# Revit family: Framery One Compact
name_source: partatom
category: Furniture Systems
units: mm (PartAtom-declared; Revit-internal decimal feet)

## family parameters
Always vertical = Yes
Cut with Voids When Loaded = No
Part Type = Normal
Room Calculation Point = No
Round Connector Dimension = Use Diameter
Shared = No
Work Plane-Based = No

## types (2) — shared parameters
Assembly Code = 5111
Keynote = 8192
Manufacturer = Framery Oy
TD_Area_ = 1.03 m²
TD_BIM_content_publish_Revit_version_ = Revit 2021.1.9
TD_BIM_content_publish_date_ = 26.02.2024
TD_Collection_name_ = Framery One Compact
TD_Depth_ = 1000 mm  [stored 3.28084 ft]
TD_Height_ = 2255 mm  [stored 7.39829 ft]
TD_Product_category_ = Office pods
TD_Weight_ = 357.00 kg
TD_Width_ = 1030 mm  [stored 3.37927 ft]
zero-valued in all types: Default Elevation

## per-type parameters (varying)
| type | Framery_Height_adjustable_seat_ | Framery_Highpower_USB_C_ | Framery_LAN_ | Model | TD_Additional_information_ |
| Base | No | No | No | One Compact Base | Exterior optional colors - extra price
Interior panel optional colors - extra price
Carpet optional colors - extra price
Sofas with optional fabrics - extra price
Table with optional surface - extra price |
| Essentials | Yes | Yes | Yes | One Compact Essentials |  |

note: [stored X ft] marks values corroborated as IEEE doubles in the binary element streams (Revit-internal decimal feet)

## geometry (parser evidence)
native form markers: Sweep x26
no freeform markers — native parametric forms only
